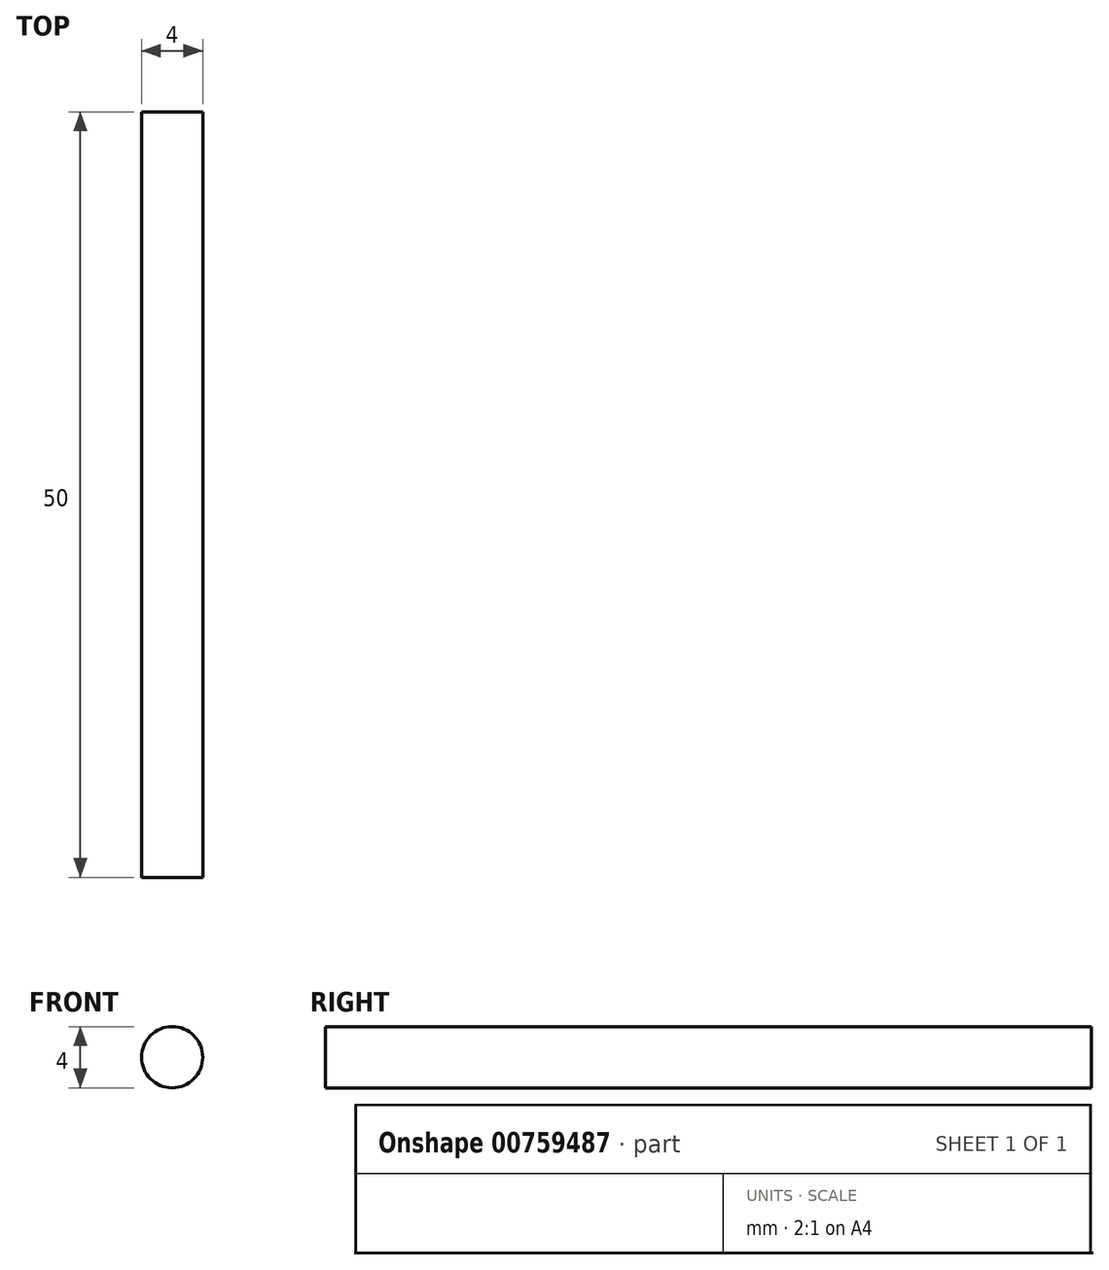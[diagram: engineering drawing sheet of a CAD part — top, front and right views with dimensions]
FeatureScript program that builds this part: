
annotation { "Feature Type Name" : "Feature", "Feature Type Description" : "" }
export const myFeature = defineFeature(function(context is Context, id is Id, definition is map)
    precondition{}
    {
        {
            var Q0;
            Q0=qCreatedBy(makeId("Front.planeOp"),FACE);
            var sketch = newSketch(context, id + "F0", { "sketchPlane" : qUnion([Q0])});
            skCircle(sketch, "E0", {"center": v(0, 0) * mm, "radius": 2 * mm});
            skSolve(sketch);
        }
        {
            var Q0;
            Q0 = qSketchRegion(id + "F0", true);
            extrude(context, id + "F1", {"entities" : qUnion([Q0]), "depth" : 50 * mm, "offsetDistance" : 25 * mm});
        }
    });
